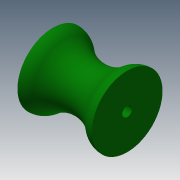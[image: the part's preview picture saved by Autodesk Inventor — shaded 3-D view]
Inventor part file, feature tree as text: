
AUTODESK INVENTOR PART (.ipt)
format: ipt  version: 2013 (Build 170138000, 138)  size: 203,776 bytes
history: native  units: mm
features: sketch x2, revolve x1, extrude x1, fillet x1
ambient origin geometry x8: Origin, YZ Plane, XZ Plane, XY Plane, X Axis, Y Axis, Z Axis, Center Point
bodies: Solid1 (feature_tree)
feature tree (5):
  revolve  "Revolution1"  [1 undecoded]
  extrude  "Extrusion1"  Depth=7.0mm
  fillet  "Fillet1"  Radius=52.7mm
  sketch  "Sketch1"  dims[d2=5.0mm d4=5.0mm]
  sketch  "Sketch2"  dims[d7=90.0deg d8=7.0mm d9=52.7mm d10=0.0mm d11=12.0mm]
note: 1 required parameter value undecoded (feature->parameter linkage not recoverable at this tier; creation-order binding heuristic only, values carry confidence <= 0.55)
